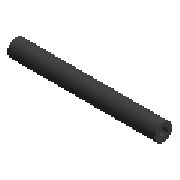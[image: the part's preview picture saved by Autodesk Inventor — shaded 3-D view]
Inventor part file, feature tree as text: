
AUTODESK INVENTOR PART (.ipt)
format: ipt  version: 2019 (Build 230136000, 136)  size: 238,080 bytes
history: native  units: mm (DEFAULTED — no unit token found)
features: other x3, sketch x2, plane x1, sweep x1
ambient origin geometry x8: Origin, YZ Plane, XZ Plane, XY Plane, X Axis, Y Axis, Z Axis, Center Point
bodies: Body1 (feature_tree)
feature tree (7):
  sketch  "Boceto 3D1"  dims[d4=10.0mm d5=10.0mm]
  other  "Punto de trabajo3"
  other  "Punto de trabajo4"
  plane  "Plano de trabajo1"
  sketch  "Boceto2"  dims[d6=0.0mm d7=0.0mm]
  other  "Punto de trabajo5"
  sweep  "Barrido1"
